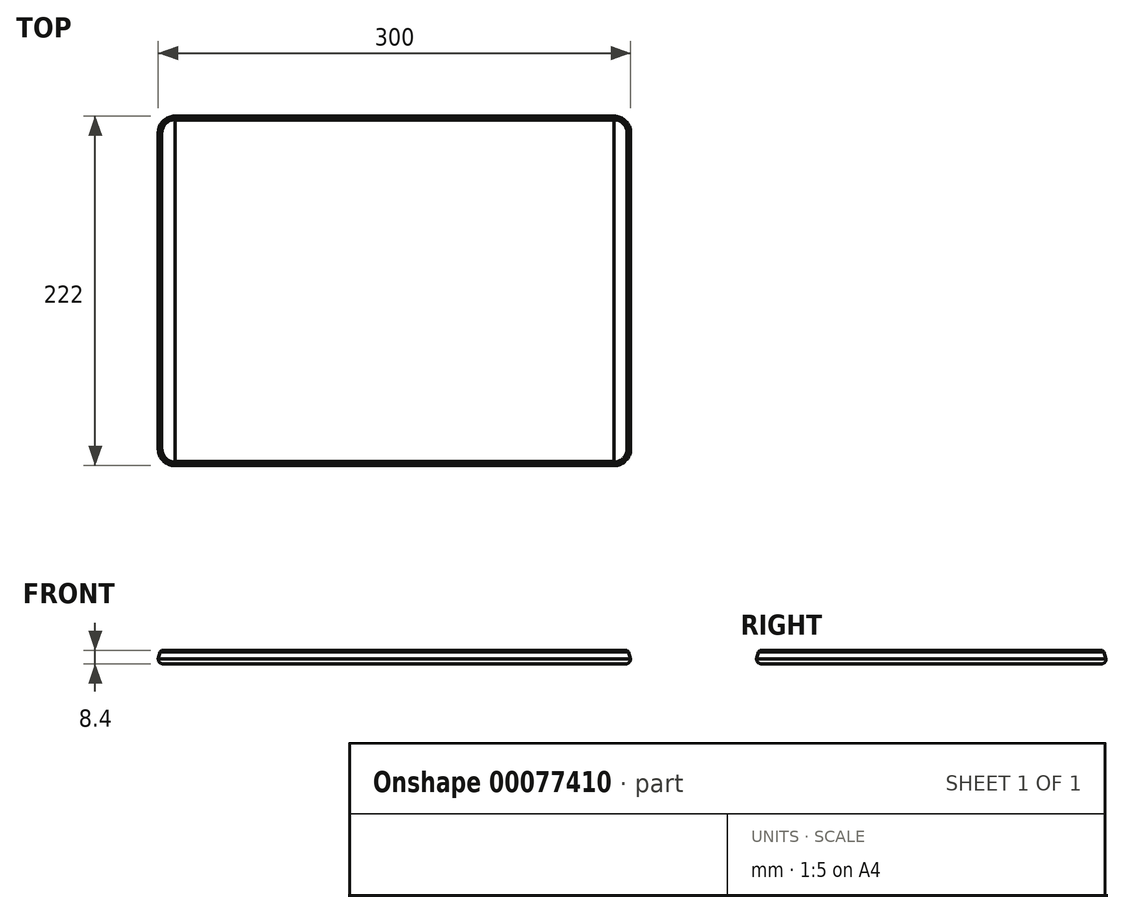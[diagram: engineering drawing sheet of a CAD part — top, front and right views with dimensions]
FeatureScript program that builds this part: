
annotation { "Feature Type Name" : "Feature", "Feature Type Description" : "" }
export const myFeature = defineFeature(function(context is Context, id is Id, definition is map)
    precondition{}
    {
        {
            var Q0;
            Q0=qCreatedBy(makeId("Top.planeOp"),FACE);
            var sketch = newSketch(context, id + "F0", { "sketchPlane" : qUnion([Q0])});
            skLineSegment(sketch, "E0", {"start": v(0, 133.33) * mm, "end": v(0, -147.92) * mm, "construction": true});
            skLineSegment(sketch, "E1", {"start": v(-190.97, 0) * mm, "end": v(249.3, 0) * mm, "construction": true});
            skLineSegment(sketch, "E2.bottom", {"start": v(-150, 111) * mm, "end": v(150, 111) * mm});
            skLineSegment(sketch, "E2.top", {"start": v(-150, -111) * mm, "end": v(150, -111) * mm});
            skLineSegment(sketch, "E2.left", {"start": v(-150, 111) * mm, "end": v(-150, -111) * mm});
            skLineSegment(sketch, "E2.right", {"start": v(150, 111) * mm, "end": v(150, -111) * mm});
            skSolve(sketch);
        }
        {
            var Q0;
            Q0=makeQuery(id+"F0.imprint","IMPRINT",FACE,{"disambiguationData":[TD([[makeQuery(id+"F0.imprint","IMPRINT",EDGE,{"derivedFrom":sQuery(id+"F0.wireOp",EDGE,"E2.bottom")}),-1.0]])]});
            extrude(context, id + "F1", {"entities" : qUnion([Q0]), "depth" : 8.4 * mm});
        }
        {
            var Q0;
            Q0=makeQuery(id+"F1.opExtrude","SWEPT_EDGE",EDGE,{"disambiguationData":[OSD([sQuery(id+"F0.wireOp",EDGE,"E2.bottom"),sQuery(id+"F0.wireOp",EDGE,"E2.left")])]});
            var Q1;
            Q1=makeQuery(id+"F1.opExtrude","SWEPT_EDGE",EDGE,{"disambiguationData":[OSD([sQuery(id+"F0.wireOp",EDGE,"E2.top"),sQuery(id+"F0.wireOp",EDGE,"E2.left")])]});
            var Q2;
            Q2=makeQuery(id+"F1.opExtrude","SWEPT_EDGE",EDGE,{"disambiguationData":[OSD([sQuery(id+"F0.wireOp",EDGE,"E2.top"),sQuery(id+"F0.wireOp",EDGE,"E2.right")])]});
            var Q3;
            Q3=makeQuery(id+"F1.opExtrude","SWEPT_EDGE",EDGE,{"disambiguationData":[OSD([sQuery(id+"F0.wireOp",EDGE,"E2.bottom"),sQuery(id+"F0.wireOp",EDGE,"E2.right")])]});
            fillet(context, id + "F2", {"entities" : qUnion([Q0, Q1, Q2, Q3]), "radius" : 10.6 * mm, "tangentPropagation" : true, "allowEdgeOverflow" : false});
        }
        {
            var Q0;
            Q0=makeQuery(id+"F1.opExtrude","CAP_EDGE",EDGE,{"disambiguationData":[OSD([sQuery(id+"F0.wireOp",EDGE,"E2.bottom")])],"isStart":true});
            var Q1;
            {var subQ0=sQuery(id+"F0.wireOp",EDGE,"E2.right");var subQ1=sQuery(id+"F0.wireOp",EDGE,"E2.bottom");Q1=makeQuery(id+"F2.opFillet","BLEND_EDGE",EDGE,{"blendedFrom":[makeQuery(id+"F1.opExtrude","SWEPT_EDGE",EDGE,{"disambiguationData":[OSD([subQ1,subQ0])]}),makeQuery(id+"F1.opExtrude","CAP_FACE",FACE,{"disambiguationData":[OSD([subQ1,sQuery(id+"F0.wireOp",EDGE,"E2.top"),sQuery(id+"F0.wireOp",EDGE,"E2.left"),subQ0])],"isStart":true})],"blendedInto":[makeQuery(id+"F1.opExtrude","CAP_FACE",FACE,{"disambiguationData":[OSD([subQ1,sQuery(id+"F0.wireOp",EDGE,"E2.top"),sQuery(id+"F0.wireOp",EDGE,"E2.left"),subQ0])],"isStart":true})]});}
            var Q2;
            Q2=makeQuery(id+"F1.opExtrude","CAP_EDGE",EDGE,{"disambiguationData":[OSD([sQuery(id+"F0.wireOp",EDGE,"E2.right")])],"isStart":true});
            fillet(context, id + "F3", {"entities" : qUnion([Q0, Q1, Q2]), "radius" : 3 * mm, "tangentPropagation" : true, "allowEdgeOverflow" : false});
        }
        {
            var Q0;
            Q0=makeQuery(id+"F1.opExtrude","CAP_EDGE",EDGE,{"disambiguationData":[OSD([sQuery(id+"F0.wireOp",EDGE,"E2.left")])],"isStart":false});
            var Q1;
            {var subQ0=sQuery(id+"F0.wireOp",EDGE,"E2.left");var subQ1=sQuery(id+"F0.wireOp",EDGE,"E2.bottom");Q1=makeQuery(id+"F2.opFillet","BLEND_EDGE",EDGE,{"blendedFrom":[makeQuery(id+"F1.opExtrude","SWEPT_EDGE",EDGE,{"disambiguationData":[OSD([subQ1,subQ0])]}),makeQuery(id+"F1.opExtrude","CAP_FACE",FACE,{"disambiguationData":[OSD([subQ1,sQuery(id+"F0.wireOp",EDGE,"E2.top"),subQ0,sQuery(id+"F0.wireOp",EDGE,"E2.right")])],"isStart":false})],"blendedInto":[makeQuery(id+"F1.opExtrude","CAP_FACE",FACE,{"disambiguationData":[OSD([subQ1,sQuery(id+"F0.wireOp",EDGE,"E2.top"),subQ0,sQuery(id+"F0.wireOp",EDGE,"E2.right")])],"isStart":false})]});}
            var Q2;
            Q2=makeQuery(id+"F1.opExtrude","CAP_EDGE",EDGE,{"disambiguationData":[OSD([sQuery(id+"F0.wireOp",EDGE,"E2.bottom")])],"isStart":false});
            chamfer(context, id + "F4", {"entities" : qUnion([Q0, Q1, Q2]), "chamferType" : ChamferType.TWO_OFFSETS, "width1" : 1.5 * mm, "oppositeDirection" : false, "width2" : 5.3 * mm, "tangentPropagation" : true});
        }
        {
            var Q0;
            {var subQ0=sQuery(id+"F0.wireOp",EDGE,"E2.bottom");Q0=makeQuery(id+"F4.opChamfer","BLEND_EDGE",EDGE,{"blendedFrom":[makeQuery(id+"F1.opExtrude","CAP_EDGE",EDGE,{"disambiguationData":[OSD([subQ0])],"isStart":false}),makeQuery(id+"F1.opExtrude","CAP_FACE",FACE,{"disambiguationData":[OSD([subQ0,sQuery(id+"F0.wireOp",EDGE,"E2.top"),sQuery(id+"F0.wireOp",EDGE,"E2.left"),sQuery(id+"F0.wireOp",EDGE,"E2.right")])],"isStart":false})],"blendedInto":[makeQuery(id+"F1.opExtrude","CAP_FACE",FACE,{"disambiguationData":[OSD([subQ0,sQuery(id+"F0.wireOp",EDGE,"E2.top"),sQuery(id+"F0.wireOp",EDGE,"E2.left"),sQuery(id+"F0.wireOp",EDGE,"E2.right")])],"isStart":false})]});}
            chamfer(context, id + "F5", {"entities" : qUnion([Q0]), "width" : 1 * mm, "tangentPropagation" : true});
        }
        {
            var Q0;
            Q0=makeQuery(id+"F1.opExtrude","CAP_FACE",FACE,{"disambiguationData":[OSD([sQuery(id+"F0.wireOp",EDGE,"E2.bottom"),sQuery(id+"F0.wireOp",EDGE,"E2.top"),sQuery(id+"F0.wireOp",EDGE,"E2.left"),sQuery(id+"F0.wireOp",EDGE,"E2.right")])],"isStart":false});
            var sketch = newSketch(context, id + "F6", { "sketchPlane" : qUnion([Q0])});
            skLineSegment(sketch, "E3.bottom", {"start": v(-139.4, 108.5) * mm, "end": v(139.4, 108.5) * mm});
            skLineSegment(sketch, "E3.top", {"start": v(-139.4, -108.5) * mm, "end": v(139.4, -108.5) * mm});
            skLineSegment(sketch, "E3.left", {"start": v(-139.4, 108.5) * mm, "end": v(-139.4, -108.5) * mm});
            skLineSegment(sketch, "E3.right", {"start": v(139.4, 108.5) * mm, "end": v(139.4, -108.5) * mm});
            skSolve(sketch);
        }
        {
            var Q0;
            Q0=makeQuery(id+"F6.imprint","IMPRINT",FACE,{"disambiguationData":[TD([[makeQuery(id+"F6.imprint","IMPRINT",EDGE,{"derivedFrom":sQuery(id+"F6.wireOp",EDGE,"E3.bottom")}),1.0]])]});
            extrude(context, id + "F7", {"entities" : qUnion([Q0]), "operationType" : NewBodyOperationType.REMOVE, "oppositeDirection" : true, "depth" : 0.1 * mm});
        }
    });
